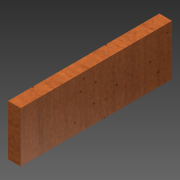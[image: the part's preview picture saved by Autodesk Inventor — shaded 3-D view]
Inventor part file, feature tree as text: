
AUTODESK INVENTOR PART (.ipt)
format: ipt  version: 2013 (Build 170138000, 138)  size: 86,016 bytes
history: native  units: in
note: dims shown in document units (in); Inventor stores cm internally (conversion verified against a paired STEP export)
features: extrude x1, sketch x1
ambient origin geometry x8: Origin, YZ Plane, XZ Plane, XY Plane, X Axis, Y Axis, Z Axis, Center Point
bodies: Solid1 (feature_tree)
feature tree (2):
  extrude  "Extrusion1"  Depth=6.0in
  sketch  "Sketch1"  dims[d0=2.0in d1=6.0in d2=0.5in d3=0.0in]
